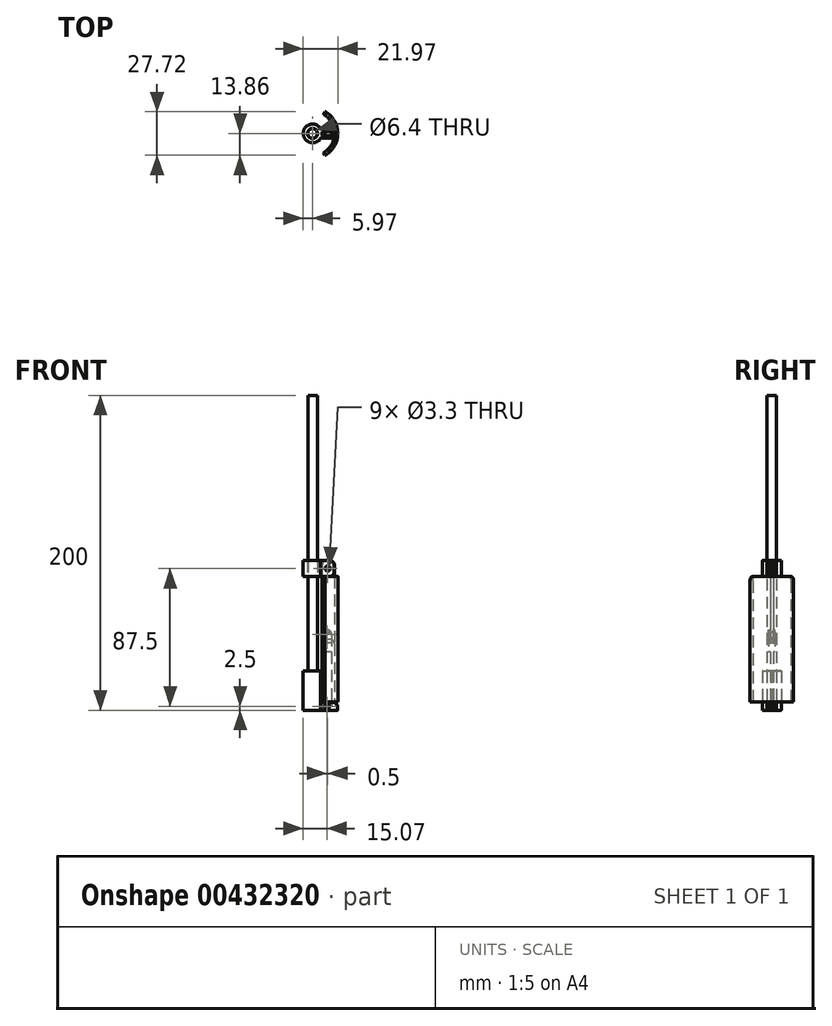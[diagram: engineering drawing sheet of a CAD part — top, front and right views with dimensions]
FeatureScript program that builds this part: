
annotation { "Feature Type Name" : "Feature", "Feature Type Description" : "" }
export const myFeature = defineFeature(function(context is Context, id is Id, definition is map)
    precondition{}
    {
        {
            var Q0;
            Q0=qCreatedBy(makeId("Top.planeOp"),FACE);
            var sketch = newSketch(context, id + "F0", { "sketchPlane" : qUnion([Q0])});
            skCircle(sketch, "E0", {"center": v(0, 0) * mm, "radius": 3 * mm});
            skCircle(sketch, "E1", {"center": v(0, 0) * mm, "radius": 16 * mm});
            skLineSegment(sketch, "E2", {"start": v(0, 0) * mm, "end": v(16, 0) * mm, "construction": true});
            skLineSegment(sketch, "E3", {"start": v(15.97, 1) * mm, "end": v(5.97, 1) * mm});
            skLineSegment(sketch, "E4", {"start": v(5.97, 1) * mm, "end": v(5.97, 0) * mm});
            skLineSegment(sketch, "E5", {"start": v(15.72, 3) * mm, "end": v(0, 3) * mm});
            skCircle(sketch, "E6", {"center": v(0, 0) * mm, "radius": 5.97 * mm});
            skLineSegment(sketch, "E7.MirrorCS", {"start": v(15.97, -1) * mm, "end": v(5.97, -1) * mm});
            skLineSegment(sketch, "E8.MirrorCS", {"start": v(5.97, -1) * mm, "end": v(5.97, 0) * mm});
            skLineSegment(sketch, "E9.MirrorCS", {"start": v(15.72, -3) * mm, "end": v(0, -3) * mm});
            skSolve(sketch);
        }
        {
            var Q0;
            Q0=makeQuery(id+"F0.imprint","IMPRINT",FACE,{"disambiguationData":[TD([[makeQuery(id+"F0.imprint","IMPRINT",EDGE,{"derivedFrom":sQuery(id+"F0.wireOp",EDGE,"E0")}),1.0]])]});
            extrude(context, id + "F1", {"entities" : qUnion([Q0]), "depth" : 200 * mm});
        }
        {
            var Q0;
            Q0=makeQuery(id+"F0.imprint","IMPRINT",FACE,{"disambiguationData":[TD([[makeQuery(id+"F0.imprint","IMPRINT",EDGE,{"derivedFrom":sQuery(id+"F0.wireOp",EDGE,"E0")}),-1.0]])]});
            var Q1;
            {var subQ0=sQuery(id+"F0.wireOp",EDGE,"E7.MirrorCS");Q1=makeQuery(id+"F0.imprint","IMPRINT",FACE,{"disambiguationData":[TD([[makeQuery(id+"F0.imprint","IMPRINT",EDGE,{"derivedFrom":subQ0}),1.0]])]});}
            var Q2;
            {var subQ5=sQuery(id+"F0.wireOp",EDGE,"E3");Q2=makeQuery(id+"F0.imprint","IMPRINT",FACE,{"disambiguationData":[TD([[makeQuery(id+"F0.imprint","IMPRINT",EDGE,{"derivedFrom":subQ5}),-1.0]])]});}
            var Q3;
            {var subQ4=sQuery(id+"F0.wireOp",EDGE,"E5");var subQ5=sQuery(id+"F0.wireOp",EDGE,"E0");var subQ6=makeQuery(id+"F0.imprint","INTERSECT",VERTEX,{"derivedFrom":[subQ5,subQ4]});Q3=makeQuery(id+"F0.imprint","IMPRINT",FACE,{"disambiguationData":[TD([[makeQuery(id+"F0.imprint","IMPRINT",EDGE,{"disambiguationData":[TD([[subQ6,1.0]])],"derivedFrom":subQ5}),-1.0]])]});}
            extrude(context, id + "F2", {"entities" : qUnion([Q0, Q1, Q2, Q3]), "operationType" : NewBodyOperationType.ADD, "depth" : 5 * mm});
        }
        {
            var Q0;
            Q0=makeQuery(id+"F2.opExtrude","CAP_FACE",FACE,{"disambiguationData":[OSD([sQuery(id+"F0.wireOp",EDGE,"E0"),sQuery(id+"F0.wireOp",EDGE,"E1")])],"isStart":false});
            var sketch = newSketch(context, id + "F3", { "sketchPlane" : qUnion([Q0])});
            skCircle(sketch, "E10", {"center": v(0, 0) * mm, "radius": 16 * mm});
            skCircle(sketch, "E11", {"center": v(0, 0) * mm, "radius": 14 * mm});
            skLineSegment(sketch, "E12", {"start": v(7, 12.12) * mm, "end": v(8, 13.86) * mm});
            skLineSegment(sketch, "E13", {"start": v(0, 0) * mm, "end": v(16, 0) * mm, "construction": true});
            skLineSegment(sketch, "E14.MirrorCS", {"start": v(7, -12.12) * mm, "end": v(8, -13.86) * mm});
            skLineSegment(sketch, "E15", {"start": v(13.97, 0.95) * mm, "end": v(6.1, 0.95) * mm});
            skLineSegment(sketch, "E16", {"start": v(6.1, 0.95) * mm, "end": v(6.1, 0) * mm});
            skLineSegment(sketch, "E17.MirrorCS", {"start": v(13.97, -0.95) * mm, "end": v(6.1, -0.95) * mm});
            skLineSegment(sketch, "E18.MirrorCS", {"start": v(6.1, -0.95) * mm, "end": v(6.1, 0) * mm});
            skLineSegment(sketch, "E19", {"start": v(12.1, 0.95) * mm, "end": v(12.1, -0.95) * mm});
            skSolve(sketch);
        }
        {
            var Q0;
            {var subQ0=sQuery(id+"F3.wireOp",EDGE,"E12");Q0=makeQuery(id+"F3.imprint","IMPRINT",FACE,{"disambiguationData":[TD([[makeQuery(id+"F3.imprint","IMPRINT",EDGE,{"derivedFrom":subQ0}),-1.0]])]});}
            var Q1;
            {var subQ3=sQuery(id+"F3.wireOp",EDGE,"E14.MirrorCS");Q1=makeQuery(id+"F3.imprint","IMPRINT",FACE,{"disambiguationData":[TD([[makeQuery(id+"F3.imprint","IMPRINT",EDGE,{"derivedFrom":subQ3}),1.0]])]});}
            var Q2;
            {var subQ0=sQuery(id+"F3.wireOp",EDGE,"E10");var subQ1=makeQuery(id+"F2.opExtrude","CAP_EDGE",EDGE,{"disambiguationData":[OSD([sQuery(id+"F0.wireOp",EDGE,"E7.MirrorCS")])],"isStart":false});var subQ2=makeQuery(id+"F3.imprint","INTERSECT",VERTEX,{"derivedFrom":[subQ1,subQ0]});Q2=makeQuery(id+"F3.imprint","IMPRINT",FACE,{"disambiguationData":[TD([[makeQuery(id+"F3.imprint","IMPRINT",EDGE,{"disambiguationData":[TD([[subQ2,1.0]])],"derivedFrom":subQ0}),1.0]])]});}
            var Q3;
            {var subQ5=makeQuery(id+"F2.opExtrude","CAP_EDGE",EDGE,{"disambiguationData":[OSD([sQuery(id+"F0.wireOp",EDGE,"E3")])],"isStart":false});var subQ7=sQuery(id+"F3.wireOp",EDGE,"E10");var subQ8=makeQuery(id+"F3.imprint","INTERSECT",VERTEX,{"derivedFrom":[subQ5,subQ7]});Q3=makeQuery(id+"F3.imprint","IMPRINT",FACE,{"disambiguationData":[TD([[makeQuery(id+"F3.imprint","IMPRINT",EDGE,{"disambiguationData":[TD([[subQ8,1.0]])],"derivedFrom":subQ7}),1.0]])]});}
            var Q4;
            {var subQ0=sQuery(id+"F3.wireOp",EDGE,"E10");var subQ1=makeQuery(id+"F2.opExtrude","CAP_EDGE",EDGE,{"disambiguationData":[OSD([sQuery(id+"F0.wireOp",EDGE,"E3")])],"isStart":false});var subQ2=makeQuery(id+"F3.imprint","INTERSECT",VERTEX,{"derivedFrom":[subQ1,subQ0]});Q4=makeQuery(id+"F3.imprint","IMPRINT",FACE,{"disambiguationData":[TD([[makeQuery(id+"F3.imprint","IMPRINT",EDGE,{"disambiguationData":[TD([[subQ2,-1.0]])],"derivedFrom":subQ0}),1.0]])]});}
            extrude(context, id + "F4", {"entities" : qUnion([Q0, Q1, Q2, Q3, Q4]), "depth" : 80 * mm, "hasSecondDirection" : true, "secondDirectionOppositeDirection" : false, "secondDirectionDepth" : .2 * mm});
        }
        {
            var Q0;
            {var subQ0=sQuery(id+"F3.wireOp",EDGE,"E15");Q0=makeQuery(id+"F3.imprint","IMPRINT",FACE,{"disambiguationData":[TD([[makeQuery(id+"F3.imprint","IMPRINT",EDGE,{"derivedFrom":subQ0}),1.0]])]});}
            var Q1;
            {var subQ3=sQuery(id+"F3.wireOp",EDGE,"E16");Q1=makeQuery(id+"F3.imprint","IMPRINT",FACE,{"disambiguationData":[TD([[makeQuery(id+"F3.imprint","IMPRINT",EDGE,{"derivedFrom":subQ3}),1.0]])]});}
            extrude(context, id + "F5", {"entities" : qUnion([Q0, Q1]), "operationType" : NewBodyOperationType.ADD, "depth" : 90 * mm});
        }
        {
            var Q0;
            {var subQ0=sQuery(id+"F3.wireOp",EDGE,"E15");Q0=makeQuery(id+"F3.imprint","IMPRINT",FACE,{"disambiguationData":[TD([[makeQuery(id+"F3.imprint","IMPRINT",EDGE,{"derivedFrom":subQ0}),1.0]])]});}
            var Q1;
            {var subQ3=sQuery(id+"F3.wireOp",EDGE,"E16");Q1=makeQuery(id+"F3.imprint","IMPRINT",FACE,{"disambiguationData":[TD([[makeQuery(id+"F3.imprint","IMPRINT",EDGE,{"derivedFrom":subQ3}),1.0]])]});}
            extrude(context, id + "F6", {"entities" : qUnion([Q0, Q1]), "operationType" : NewBodyOperationType.REMOVE, "depth" : 40 * mm});
        }
        {
            var Q0;
            {var subQ3=sQuery(id+"F3.wireOp",EDGE,"E16");Q0=makeQuery(id+"F3.imprint","IMPRINT",FACE,{"disambiguationData":[TD([[makeQuery(id+"F3.imprint","IMPRINT",EDGE,{"derivedFrom":subQ3}),1.0]])]});}
            extrude(context, id + "F7", {"entities" : qUnion([Q0]), "depth" : 38 * mm, "hasSecondDirection" : true, "secondDirectionOppositeDirection" : true, "secondDirectionDepth" : 5 * mm});
        }
        {
            var Q0;
            Q0=makeQuery(id+"F2.opExtrude","CAP_FACE",FACE,{"disambiguationData":[OSD([sQuery(id+"F0.wireOp",EDGE,"E0"),sQuery(id+"F0.wireOp",EDGE,"E1")])],"isStart":false});
            var sketch = newSketch(context, id + "F8", { "sketchPlane" : qUnion([Q0])});
            skLineSegment(sketch, "E20", {"start": v(14, 0) * mm, "end": v(14, 1) * mm, "construction": true});
            skLineSegment(sketch, "E21", {"start": v(14, 1) * mm, "end": v(6, 1) * mm});
            skLineSegment(sketch, "E22", {"start": v(6, 1) * mm, "end": v(6, 0) * mm});
            skLineSegment(sketch, "E23", {"start": v(14, 1) * mm, "end": v(14, 3) * mm});
            skLineSegment(sketch, "E24", {"start": v(0, 3) * mm, "end": v(0, 0) * mm});
            skLineSegment(sketch, "E25", {"start": v(14, 3) * mm, "end": v(6, 3) * mm});
            skLineSegment(sketch, "E26", {"start": v(6, 3) * mm, "end": v(0, 3) * mm});
            skPoint(sketch, "E27", {"position": v(10, 3) * mm});
            skLineSegment(sketch, "E28", {"start": v(0, 0) * mm, "end": v(6, 0) * mm, "construction": true});
            skLineSegment(sketch, "E29.MirrorCS", {"start": v(6, -1) * mm, "end": v(6, 0) * mm});
            skLineSegment(sketch, "E30.MirrorCS", {"start": v(14, -1) * mm, "end": v(6, -1) * mm});
            skLineSegment(sketch, "E31.MirrorCS", {"start": v(14, -1) * mm, "end": v(14, -3) * mm});
            skLineSegment(sketch, "E32.MirrorCS", {"start": v(14, -3) * mm, "end": v(6, -3) * mm});
            skLineSegment(sketch, "E33.MirrorCS", {"start": v(6, -3) * mm, "end": v(0, -3) * mm});
            skLineSegment(sketch, "E34.MirrorCS", {"start": v(0, -3) * mm, "end": v(0, 0) * mm});
            skCircle(sketch, "E35", {"center": v(0, 0) * mm, "radius": 14 * mm});
            skCircle(sketch, "E36", {"center": v(0, 0) * mm, "radius": 3.2 * mm});
            skLineSegment(sketch, "E37", {"start": v(6, 3) * mm, "end": v(6, 1) * mm});
            skLineSegment(sketch, "E38.MirrorCS", {"start": v(6, -3) * mm, "end": v(6, -1) * mm});
            skCircle(sketch, "E39", {"center": v(0, 0) * mm, "radius": 6 * mm});
            skSolve(sketch);
        }
        {
            var Q0;
            {var subQ0=sQuery(id+"F8.wireOp",EDGE,"E38.MirrorCS");Q0=makeQuery(id+"F8.imprint","IMPRINT",FACE,{"disambiguationData":[TD([[makeQuery(id+"F8.imprint","IMPRINT",EDGE,{"derivedFrom":subQ0}),-1.0]])]});}
            var Q1;
            {var subQ0=sQuery(id+"F8.wireOp",EDGE,"E38.MirrorCS");Q1=makeQuery(id+"F8.imprint","IMPRINT",FACE,{"disambiguationData":[TD([[makeQuery(id+"F8.imprint","IMPRINT",EDGE,{"derivedFrom":subQ0}),1.0]])]});}
            var Q2;
            {var subQ1=makeQuery(id+"F2.opExtrude","CAP_EDGE",EDGE,{"disambiguationData":[OSD([sQuery(id+"F0.wireOp",EDGE,"E6")])],"isStart":false});var subQ5=sQuery(id+"F8.wireOp",EDGE,"E26");var subQ6=makeQuery(id+"F8.imprint","INTERSECT",VERTEX,{"derivedFrom":[subQ1,subQ5]});Q2=makeQuery(id+"F8.imprint","IMPRINT",FACE,{"disambiguationData":[TD([[makeQuery(id+"F8.imprint","IMPRINT",EDGE,{"disambiguationData":[TD([[subQ6,-1.0]])],"derivedFrom":subQ5}),1.0]])]});}
            var Q3;
            {var subQ1=makeQuery(id+"F2.opExtrude","CAP_EDGE",EDGE,{"disambiguationData":[OSD([sQuery(id+"F0.wireOp",EDGE,"E6")])],"isStart":false});Q3=makeQuery(id+"F8.imprint","IMPRINT",FACE,{"disambiguationData":[TD([[makeQuery(id+"F8.imprint","IMPRINT",EDGE,{"derivedFrom":subQ1}),1.0]])]});}
            var Q4;
            {var subQ0=sQuery(id+"F8.wireOp",EDGE,"E37");Q4=makeQuery(id+"F8.imprint","IMPRINT",FACE,{"disambiguationData":[TD([[makeQuery(id+"F8.imprint","IMPRINT",EDGE,{"derivedFrom":subQ0}),1.0]])]});}
            var Q5;
            {var subQ3=sQuery(id+"F8.wireOp",EDGE,"E37");Q5=makeQuery(id+"F8.imprint","IMPRINT",FACE,{"disambiguationData":[TD([[makeQuery(id+"F8.imprint","IMPRINT",EDGE,{"derivedFrom":subQ3}),-1.0]])]});}
            extrude(context, id + "F9", {"entities" : qUnion([Q0, Q1, Q2, Q3, Q4, Q5]), "depth" : 10 * mm});
        }
        {
            var Q0;
            Q0=makeQuery(id+"F9.opExtrude","SWEPT_BODY",BODY,{"disambiguationData":[OSD([sQuery(id+"F8.wireOp",EDGE,"E21"),sQuery(id+"F8.wireOp",EDGE,"E22"),sQuery(id+"F8.wireOp",EDGE,"E24"),sQuery(id+"F8.wireOp",EDGE,"E25"),sQuery(id+"F8.wireOp",EDGE,"E26"),sQuery(id+"F8.wireOp",EDGE,"E29.MirrorCS"),sQuery(id+"F8.wireOp",EDGE,"E30.MirrorCS"),sQuery(id+"F8.wireOp",EDGE,"E32.MirrorCS"),sQuery(id+"F8.wireOp",EDGE,"E33.MirrorCS"),sQuery(id+"F8.wireOp",EDGE,"E34.MirrorCS"),sQuery(id+"F8.wireOp",EDGE,"E35"),sQuery(id+"F8.wireOp",EDGE,"E36")])]});
            transform(context, id + "F10", {"entities" : qUnion([Q0]), "transformType" : TransformType.TRANSLATION_3D, "dx" : 0 * mm, "dy" : 0 * mm, "dz" : 80 * mm, "makeCopy" : false});
        }
        {
            var Q0;
            Q0=makeQuery(id+"F7.opExtrude","SWEPT_FACE",FACE,{"disambiguationData":[OSD([sQuery(id+"F3.wireOp",EDGE,"E15")])]});
            var sketch = newSketch(context, id + "F11", { "sketchPlane" : qUnion([Q0])});
            skLineSegment(sketch, "E40", {"start": v(-12.1, 37) * mm, "end": v(-6.1, 37) * mm});
            skSolve(sketch);
        }
        {
            var Q0;
            {var subQ0=sQuery(id+"F11.wireOp",EDGE,"E40");Q0=makeQuery(id+"F11.imprint","IMPRINT",FACE,{"disambiguationData":[TD([[makeQuery(id+"F11.imprint","IMPRINT",EDGE,{"derivedFrom":subQ0}),1.0]])]});}
            extrude(context, id + "F12", {"entities" : qUnion([Q0]), "operationType" : NewBodyOperationType.ADD, "depth" : 1 * mm, "hasSecondDirection" : true, "secondDirectionOppositeDirection" : true, "secondDirectionDepth" : 3 * mm});
        }
        {
            var Q0;
            {var subQ0=sQuery(id+"F3.wireOp",EDGE,"E15");Q0=makeQuery(id+"F12.boolean.opBoolean","MERGE",FACE,{"derivedFrom":[makeQuery(id+"F7.opExtrude","CAP_FACE",FACE,{"disambiguationData":[OSD([subQ0,sQuery(id+"F3.wireOp",EDGE,"E16"),sQuery(id+"F3.wireOp",EDGE,"E17.MirrorCS"),sQuery(id+"F3.wireOp",EDGE,"E18.MirrorCS"),sQuery(id+"F3.wireOp",EDGE,"E19")])],"isStart":false}),makeQuery(id+"F12.opExtrude","SWEPT_FACE",FACE,{"disambiguationData":[OSD([subQ0])]})]});}
            var sketch = newSketch(context, id + "F13", { "sketchPlane" : qUnion([Q0])});
            skLineSegment(sketch, "E41", {"start": v(6.1, 1.05) * mm, "end": v(12.1, 1.05) * mm});
            skLineSegment(sketch, "E42", {"start": v(6.1, -0.05) * mm, "end": v(12.1, -0.05) * mm, "construction": true});
            skLineSegment(sketch, "E43.MirrorCS", {"start": v(6.1, -1.15) * mm, "end": v(12.1, -1.15) * mm});
            skSolve(sketch);
        }
        {
            var Q0;
            {var subQ0=sQuery(id+"F13.wireOp",EDGE,"E41");Q0=makeQuery(id+"F13.imprint","IMPRINT",FACE,{"disambiguationData":[TD([[makeQuery(id+"F13.imprint","IMPRINT",EDGE,{"derivedFrom":subQ0}),1.0]])]});}
            var Q1;
            {var subQ0=sQuery(id+"F13.wireOp",EDGE,"E43.MirrorCS");Q1=makeQuery(id+"F13.imprint","IMPRINT",FACE,{"disambiguationData":[TD([[makeQuery(id+"F13.imprint","IMPRINT",EDGE,{"derivedFrom":subQ0}),-1.0]])]});}
            extrude(context, id + "F14", {"entities" : qUnion([Q0, Q1]), "operationType" : NewBodyOperationType.ADD, "depth" : 8 * mm});
        }
        {
            var Q0;
            {var subQ0=sQuery(id+"F3.wireOp",EDGE,"E15");Q0=makeQuery(id+"F14.boolean.opBoolean","MERGE",FACE,{"derivedFrom":[makeQuery(id+"F12.opExtrude","CAP_FACE",FACE,{"disambiguationData":[OSD([subQ0,sQuery(id+"F3.wireOp",EDGE,"E16"),sQuery(id+"F3.wireOp",EDGE,"E19"),sQuery(id+"F11.wireOp",EDGE,"E40")])],"isStart":false}),makeQuery(id+"F14.opExtrude","SWEPT_FACE",FACE,{"disambiguationData":[OSD([subQ0]),TDD([makeQuery(id+"F13.imprint","IMPRINT",EDGE,{"derivedFrom":makeQuery(id+"F12.opExtrude","CAP_EDGE",EDGE,{"disambiguationData":[OSD([subQ0])],"isStart":false})})])]})]});}
            var sketch = newSketch(context, id + "F15", { "sketchPlane" : qUnion([Q0])});
            skPoint(sketch, "E44", {"position": v(-9.1, 48) * mm});
            skPoint(sketch, "E44.positionSnap0", {"position": v(-9.1, 51) * mm});
            skSolve(sketch);
        }
        {
            var Q0;
            Q0=sQuery(id+"F15.wireOp",VERTEX,"E44");
            var Q1;
            Q1=makeQuery(id+"F7.opExtrude","SWEPT_BODY",BODY,{"disambiguationData":[OSD([sQuery(id+"F3.wireOp",EDGE,"E15"),sQuery(id+"F3.wireOp",EDGE,"E16"),sQuery(id+"F3.wireOp",EDGE,"E17.MirrorCS"),sQuery(id+"F3.wireOp",EDGE,"E18.MirrorCS"),sQuery(id+"F3.wireOp",EDGE,"E19")])]});
            hole(context, id + "F16", {"style" : HoleStyle.SIMPLE, "endStyle" : HoleEndStyle.THROUGH, "standardTappedOrClearance" : lookupTablePath({ "standard" : "ISO", "fit" : "Normal", "size" : "M3", "type" : "Clearance" }), "standardBlindInLast" : lookupTablePath({ "fit" : "Standard", "standard" : "ISO", "size" : "M3", "type" : "Clearance" }), "holeDiameter" : 3.3 * mm, "isTappedThrough" : true, "tappedDepth" : 12 * mm, "tapClearance" : 3, "locations" : qUnion([Q0]), "scope" : qUnion([Q1])});
        }
        {
            var Q0;
            Q0=makeQuery(id+"F0.imprint","IMPRINT",FACE,{"disambiguationData":[TD([[makeQuery(id+"F0.imprint","IMPRINT",EDGE,{"derivedFrom":sQuery(id+"F0.wireOp",EDGE,"E0")}),-1.0]])]});
            var sketch = newSketch(context, id + "F17", { "sketchPlane" : qUnion([Q0])});
            skLineSegment(sketch, "E45", {"start": v(0, 0) * mm, "end": v(16, 0) * mm});
            skLineSegment(sketch, "E46", {"start": v(16, 0) * mm, "end": v(16, -1) * mm});
            skLineSegment(sketch, "E47", {"start": v(16, -1) * mm, "end": v(6, -1) * mm});
            skLineSegment(sketch, "E48", {"start": v(6, -1) * mm, "end": v(6, 0) * mm});
            skLineSegment(sketch, "E49.MirrorCS", {"start": v(6, 1) * mm, "end": v(6, 0) * mm});
            skLineSegment(sketch, "E50.MirrorCS", {"start": v(16, 1) * mm, "end": v(6, 1) * mm});
            skLineSegment(sketch, "E51.MirrorCS", {"start": v(16, 0) * mm, "end": v(16, 1) * mm});
            skSolve(sketch);
        }
        {
            var Q0;
            {var subQ3=sQuery(id+"F17.wireOp",EDGE,"E48");Q0=makeQuery(id+"F17.imprint","IMPRINT",FACE,{"disambiguationData":[TD([[makeQuery(id+"F17.imprint","IMPRINT",EDGE,{"derivedFrom":subQ3}),-1.0]])]});}
            var Q1;
            {var subQ3=sQuery(id+"F17.wireOp",EDGE,"E49.MirrorCS");Q1=makeQuery(id+"F17.imprint","IMPRINT",FACE,{"disambiguationData":[TD([[makeQuery(id+"F17.imprint","IMPRINT",EDGE,{"derivedFrom":subQ3}),1.0]])]});}
            extrude(context, id + "F18", {"entities" : qUnion([Q0, Q1]), "depth" : 6 * mm});
        }
        {
            var Q0;
            Q0=makeQuery(id+"F18.opExtrude","SWEPT_BODY",BODY,{"disambiguationData":[OSD([sQuery(id+"F0.wireOp",EDGE,"E1"),sQuery(id+"F17.wireOp",EDGE,"E47"),sQuery(id+"F17.wireOp",EDGE,"E48"),sQuery(id+"F17.wireOp",EDGE,"E49.MirrorCS"),sQuery(id+"F17.wireOp",EDGE,"E50.MirrorCS")])]});
            var Q1;
            Q1=makeQuery(id+"F1.opExtrude","SWEPT_BODY",BODY,{"disambiguationData":[OSD([sQuery(id+"F0.wireOp",EDGE,"E0")])]});
            booleanBodies(context, id + "F19", {"operationType" : BooleanOperationType.SUBTRACTION, "tools" : qUnion([Q0]), "targets" : qUnion([Q1])});
        }
        {
            var Q0;
            Q0=makeQuery(id+"F7.opExtrude","SWEPT_FACE",FACE,{"disambiguationData":[OSD([sQuery(id+"F3.wireOp",EDGE,"E17.MirrorCS")])]});
            var sketch = newSketch(context, id + "F20", { "sketchPlane" : qUnion([Q0])});
            skPoint(sketch, "E52", {"position": v(9.1, 0) * mm});
            skPoint(sketch, "E53", {"position": v(9.1, 2.5) * mm});
            skSolve(sketch);
        }
        {
            var Q0;
            Q0=sQuery(id+"F20.wireOp",VERTEX,"E53");
            var Q1;
            Q1=makeQuery(id+"F7.opExtrude","SWEPT_BODY",BODY,{"disambiguationData":[OSD([sQuery(id+"F3.wireOp",EDGE,"E15"),sQuery(id+"F3.wireOp",EDGE,"E16"),sQuery(id+"F3.wireOp",EDGE,"E17.MirrorCS"),sQuery(id+"F3.wireOp",EDGE,"E18.MirrorCS"),sQuery(id+"F3.wireOp",EDGE,"E19")])]});
            hole(context, id + "F21", {"style" : HoleStyle.SIMPLE, "endStyle" : HoleEndStyle.THROUGH, "standardTappedOrClearance" : lookupTablePath({ "standard" : "ISO", "fit" : "Normal", "size" : "M3", "type" : "Clearance" }), "standardBlindInLast" : lookupTablePath({ "fit" : "Standard", "standard" : "ISO", "size" : "M3", "type" : "Clearance" }), "holeDiameter" : 3.3 * mm, "isTappedThrough" : true, "tappedDepth" : 12 * mm, "tapClearance" : 3, "locations" : qUnion([Q0]), "scope" : qUnion([Q1])});
        }
        {
            var Q0;
            Q0=sQuery(id+"F20.wireOp",VERTEX,"E53");
            var Q1;
            Q1=makeQuery(id+"F1.opExtrude","SWEPT_BODY",BODY,{"disambiguationData":[OSD([sQuery(id+"F0.wireOp",EDGE,"E0")])]});
            hole(context, id + "F22", {"style" : HoleStyle.SIMPLE, "endStyle" : HoleEndStyle.THROUGH, "standardTappedOrClearance" : lookupTablePath({ "standard" : "ISO", "fit" : "Normal", "size" : "M3", "type" : "Clearance" }), "standardBlindInLast" : lookupTablePath({ "fit" : "Standard", "standard" : "ISO", "size" : "M3", "type" : "Clearance" }), "holeDiameter" : 3.3 * mm, "isTappedThrough" : true, "tappedDepth" : 12 * mm, "tapClearance" : 3, "locations" : qUnion([Q0]), "scope" : qUnion([Q1])});
        }
        {
            var Q0;
            Q0=sQuery(id+"F20.wireOp",VERTEX,"E53");
            var Q1;
            Q1=makeQuery(id+"F1.opExtrude","SWEPT_BODY",BODY,{"disambiguationData":[OSD([sQuery(id+"F0.wireOp",EDGE,"E0")])]});
            hole(context, id + "F23", {"style" : HoleStyle.SIMPLE, "endStyle" : HoleEndStyle.THROUGH, "oppositeDirection" : true, "standardTappedOrClearance" : lookupTablePath({ "standard" : "ISO", "fit" : "Normal", "size" : "M3", "type" : "Clearance" }), "standardBlindInLast" : lookupTablePath({ "fit" : "Standard", "standard" : "ISO", "size" : "M3", "type" : "Clearance" }), "holeDiameter" : 3.3 * mm, "isTappedThrough" : true, "tappedDepth" : 12 * mm, "tapClearance" : 3, "locations" : qUnion([Q0]), "scope" : qUnion([Q1])});
        }
        {
            var Q0;
            Q0=sQuery(id+"F15.wireOp",VERTEX,"E44");
            var Q1;
            Q1=makeQuery(id+"F4.opExtrude","SWEPT_BODY",BODY,{"disambiguationData":[OSD([sQuery(id+"F3.wireOp",EDGE,"E10"),sQuery(id+"F3.wireOp",EDGE,"E11"),sQuery(id+"F3.wireOp",EDGE,"E12"),sQuery(id+"F3.wireOp",EDGE,"E14.MirrorCS")])]});
            hole(context, id + "F24", {"style" : HoleStyle.SIMPLE, "endStyle" : HoleEndStyle.BLIND, "standardTappedOrClearance" : lookupTablePath({ "standard" : "ISO", "fit" : "Normal", "size" : "M3", "type" : "Clearance" }), "standardBlindInLast" : lookupTablePath({ "fit" : "Standard", "standard" : "ISO", "size" : "M3", "type" : "Clearance" }), "holeDiameter" : 3.3 * mm, "holeDepth" : 6 * mm, "isTappedThrough" : true, "tappedDepth" : 12 * mm, "tapClearance" : 3, "locations" : qUnion([Q0]), "scope" : qUnion([Q1])});
        }
        {
            var Q0;
            Q0=makeQuery(id+"F5.opExtrude","SWEPT_FACE",FACE,{"disambiguationData":[OSD([sQuery(id+"F3.wireOp",EDGE,"E17.MirrorCS")])]});
            var sketch = newSketch(context, id + "F25", { "sketchPlane" : qUnion([Q0])});
            skPoint(sketch, "E54", {"position": v(9.6, 90) * mm});
            skSolve(sketch);
        }
        {
            var Q0;
            Q0=sQuery(id+"F25.wireOp",VERTEX,"E54");
            var Q1;
            Q1=makeQuery(id+"F9.opExtrude","SWEPT_BODY",BODY,{"disambiguationData":[OSD([sQuery(id+"F0.wireOp",EDGE,"E3"),sQuery(id+"F0.wireOp",EDGE,"E4"),sQuery(id+"F0.wireOp",EDGE,"E6"),sQuery(id+"F0.wireOp",EDGE,"E7.MirrorCS"),sQuery(id+"F0.wireOp",EDGE,"E8.MirrorCS"),sQuery(id+"F8.wireOp",EDGE,"E21"),sQuery(id+"F8.wireOp",EDGE,"E25"),sQuery(id+"F8.wireOp",EDGE,"E26"),sQuery(id+"F8.wireOp",EDGE,"E30.MirrorCS"),sQuery(id+"F8.wireOp",EDGE,"E32.MirrorCS"),sQuery(id+"F8.wireOp",EDGE,"E33.MirrorCS"),sQuery(id+"F8.wireOp",EDGE,"E35"),sQuery(id+"F8.wireOp",EDGE,"E36")])]});
            hole(context, id + "F26", {"style" : HoleStyle.SIMPLE, "endStyle" : HoleEndStyle.BLIND, "standardTappedOrClearance" : lookupTablePath({ "standard" : "ISO", "fit" : "Normal", "size" : "M3", "type" : "Clearance" }), "standardBlindInLast" : lookupTablePath({ "fit" : "Standard", "standard" : "ISO", "size" : "M3", "type" : "Clearance" }), "holeDiameter" : 3.3 * mm, "holeDepth" : 6 * mm, "isTappedThrough" : true, "tappedDepth" : 12 * mm, "tapClearance" : 3, "locations" : qUnion([Q0]), "scope" : qUnion([Q1])});
        }
        {
            var Q0;
            Q0=sQuery(id+"F25.wireOp",VERTEX,"E54");
            var Q1;
            Q1=makeQuery(id+"F9.opExtrude","SWEPT_BODY",BODY,{"disambiguationData":[OSD([sQuery(id+"F0.wireOp",EDGE,"E3"),sQuery(id+"F0.wireOp",EDGE,"E4"),sQuery(id+"F0.wireOp",EDGE,"E6"),sQuery(id+"F0.wireOp",EDGE,"E7.MirrorCS"),sQuery(id+"F0.wireOp",EDGE,"E8.MirrorCS"),sQuery(id+"F8.wireOp",EDGE,"E21"),sQuery(id+"F8.wireOp",EDGE,"E25"),sQuery(id+"F8.wireOp",EDGE,"E26"),sQuery(id+"F8.wireOp",EDGE,"E30.MirrorCS"),sQuery(id+"F8.wireOp",EDGE,"E32.MirrorCS"),sQuery(id+"F8.wireOp",EDGE,"E33.MirrorCS"),sQuery(id+"F8.wireOp",EDGE,"E35"),sQuery(id+"F8.wireOp",EDGE,"E36")])]});
            hole(context, id + "F27", {"style" : HoleStyle.SIMPLE, "endStyle" : HoleEndStyle.BLIND, "oppositeDirection" : true, "standardTappedOrClearance" : lookupTablePath({ "standard" : "ISO", "fit" : "Normal", "size" : "M3", "type" : "Clearance" }), "standardBlindInLast" : lookupTablePath({ "fit" : "Standard", "standard" : "ISO", "size" : "M3", "type" : "Clearance" }), "holeDiameter" : 3.3 * mm, "holeDepth" : 6 * mm, "isTappedThrough" : true, "tappedDepth" : 12 * mm, "tapClearance" : 3, "locations" : qUnion([Q0]), "scope" : qUnion([Q1])});
        }
        {
            var Q0;
            Q0=sQuery(id+"F25.wireOp",VERTEX,"E54");
            var Q1;
            Q1=makeQuery(id+"F4.opExtrude","SWEPT_BODY",BODY,{"disambiguationData":[OSD([sQuery(id+"F3.wireOp",EDGE,"E10"),sQuery(id+"F3.wireOp",EDGE,"E11"),sQuery(id+"F3.wireOp",EDGE,"E12"),sQuery(id+"F3.wireOp",EDGE,"E14.MirrorCS")])]});
            hole(context, id + "F28", {"style" : HoleStyle.SIMPLE, "endStyle" : HoleEndStyle.BLIND, "standardTappedOrClearance" : lookupTablePath({ "standard" : "ISO", "fit" : "Normal", "size" : "M3", "type" : "Clearance" }), "standardBlindInLast" : lookupTablePath({ "fit" : "Standard", "standard" : "ISO", "size" : "M3", "type" : "Clearance" }), "holeDiameter" : 3.3 * mm, "holeDepth" : 6 * mm, "isTappedThrough" : true, "tappedDepth" : 12 * mm, "tapClearance" : 3, "locations" : qUnion([Q0]), "scope" : qUnion([Q1])});
        }
        {
            var Q0;
            Q0=makeQuery(id+"F5.opExtrude","CAP_EDGE",EDGE,{"disambiguationData":[OSD([sQuery(id+"F3.wireOp",EDGE,"E11")])],"isStart":false});
            var Q1;
            Q1=makeQuery(id+"F5.opExtrude","CAP_EDGE",EDGE,{"disambiguationData":[OSD([sQuery(id+"F3.wireOp",EDGE,"E16"),sQuery(id+"F3.wireOp",EDGE,"E18.MirrorCS")])],"isStart":false});
            var Q2;
            {var subQ0=sQuery(id+"F8.wireOp",EDGE,"E35");Q2=makeQuery(id+"F9.opExtrude","CAP_EDGE",EDGE,{"disambiguationData":[OSD([subQ0]),TDD([makeQuery(id+"F8.imprint","IMPRINT",EDGE,{"disambiguationData":[TD([[makeQuery(id+"F8.imprint","INTERSECT",VERTEX,{"derivedFrom":[sQuery(id+"F8.wireOp",EDGE,"E30.MirrorCS"),subQ0]}),1.0]])],"derivedFrom":subQ0})])],"isStart":false});}
            var Q3;
            {var subQ0=sQuery(id+"F8.wireOp",EDGE,"E35");Q3=makeQuery(id+"F9.opExtrude","CAP_EDGE",EDGE,{"disambiguationData":[OSD([subQ0]),TDD([makeQuery(id+"F8.imprint","IMPRINT",EDGE,{"disambiguationData":[TD([[makeQuery(id+"F8.imprint","INTERSECT",VERTEX,{"derivedFrom":[sQuery(id+"F8.wireOp",EDGE,"E21"),subQ0]}),-1.0]])],"derivedFrom":subQ0})])],"isStart":false});}
            var Q4;
            {var subQ0=sQuery(id+"F8.wireOp",EDGE,"E35");Q4=makeQuery(id+"F9.opExtrude","CAP_EDGE",EDGE,{"disambiguationData":[OSD([subQ0]),TDD([makeQuery(id+"F8.imprint","IMPRINT",EDGE,{"disambiguationData":[TD([[makeQuery(id+"F8.imprint","INTERSECT",VERTEX,{"derivedFrom":[sQuery(id+"F8.wireOp",EDGE,"E30.MirrorCS"),subQ0]}),1.0]])],"derivedFrom":subQ0})])],"isStart":true});}
            var Q5;
            {var subQ0=sQuery(id+"F8.wireOp",EDGE,"E35");Q5=makeQuery(id+"F9.opExtrude","CAP_EDGE",EDGE,{"disambiguationData":[OSD([subQ0]),TDD([makeQuery(id+"F8.imprint","IMPRINT",EDGE,{"disambiguationData":[TD([[makeQuery(id+"F8.imprint","INTERSECT",VERTEX,{"derivedFrom":[sQuery(id+"F8.wireOp",EDGE,"E21"),subQ0]}),-1.0]])],"derivedFrom":subQ0})])],"isStart":true});}
            var Q6;
            {var subQ0=sQuery(id+"F3.wireOp",EDGE,"E16");var subQ1=sQuery(id+"F3.wireOp",EDGE,"E15");var subQ2=sQuery(id+"F3.wireOp",EDGE,"E18.MirrorCS");var subQ3=makeQuery(id+"F12.boolean.opBoolean","MERGE",EDGE,{"derivedFrom":[makeQuery(id+"F7.opExtrude","CAP_EDGE",EDGE,{"disambiguationData":[OSD([subQ0,subQ2])],"isStart":false}),makeQuery(id+"F12.opExtrude","SWEPT_EDGE",EDGE,{"disambiguationData":[OSD([subQ1,subQ0])]})]});Q6=makeQuery(id+"F14.opExtrude","CAP_EDGE",EDGE,{"disambiguationData":[OSD([subQ1,subQ0,subQ2]),TDD([makeQuery(id+"F13.imprint","IMPRINT",EDGE,{"disambiguationData":[TD([[makeQuery(id+"F13.imprint","INTERSECT",VERTEX,{"derivedFrom":[makeQuery(id+"F12.opExtrude","CAP_EDGE",EDGE,{"disambiguationData":[OSD([subQ1])],"isStart":true}),subQ3]}),1.0]])],"derivedFrom":subQ3})])],"isStart":false});}
            var Q7;
            {var subQ0=sQuery(id+"F3.wireOp",EDGE,"E19");var subQ1=sQuery(id+"F3.wireOp",EDGE,"E15");var subQ2=makeQuery(id+"F12.boolean.opBoolean","MERGE",EDGE,{"derivedFrom":[makeQuery(id+"F7.opExtrude","CAP_EDGE",EDGE,{"disambiguationData":[OSD([subQ0])],"isStart":false}),makeQuery(id+"F12.opExtrude","SWEPT_EDGE",EDGE,{"disambiguationData":[OSD([subQ1,subQ0])]})]});Q7=makeQuery(id+"F14.opExtrude","CAP_EDGE",EDGE,{"disambiguationData":[OSD([subQ1,subQ0]),TDD([makeQuery(id+"F13.imprint","IMPRINT",EDGE,{"disambiguationData":[TD([[makeQuery(id+"F13.imprint","INTERSECT",VERTEX,{"derivedFrom":[makeQuery(id+"F12.opExtrude","CAP_EDGE",EDGE,{"disambiguationData":[OSD([subQ1])],"isStart":true}),subQ2]}),1.0]])],"derivedFrom":subQ2})])],"isStart":false});}
            var Q8;
            {var subQ0=sQuery(id+"F3.wireOp",EDGE,"E19");var subQ1=sQuery(id+"F3.wireOp",EDGE,"E15");var subQ2=makeQuery(id+"F12.boolean.opBoolean","MERGE",EDGE,{"derivedFrom":[makeQuery(id+"F7.opExtrude","CAP_EDGE",EDGE,{"disambiguationData":[OSD([subQ0])],"isStart":false}),makeQuery(id+"F12.opExtrude","SWEPT_EDGE",EDGE,{"disambiguationData":[OSD([subQ1,subQ0])]})]});Q8=makeQuery(id+"F14.opExtrude","CAP_EDGE",EDGE,{"disambiguationData":[OSD([subQ1,subQ0]),TDD([makeQuery(id+"F13.imprint","IMPRINT",EDGE,{"disambiguationData":[TD([[makeQuery(id+"F13.imprint","INTERSECT",VERTEX,{"derivedFrom":[makeQuery(id+"F12.opExtrude","CAP_EDGE",EDGE,{"disambiguationData":[OSD([subQ1])],"isStart":false}),subQ2]}),-1.0]])],"derivedFrom":subQ2})])],"isStart":false});}
            var Q9;
            {var subQ0=sQuery(id+"F3.wireOp",EDGE,"E16");var subQ1=sQuery(id+"F3.wireOp",EDGE,"E15");var subQ2=sQuery(id+"F3.wireOp",EDGE,"E18.MirrorCS");var subQ3=makeQuery(id+"F12.boolean.opBoolean","MERGE",EDGE,{"derivedFrom":[makeQuery(id+"F7.opExtrude","CAP_EDGE",EDGE,{"disambiguationData":[OSD([subQ0,subQ2])],"isStart":false}),makeQuery(id+"F12.opExtrude","SWEPT_EDGE",EDGE,{"disambiguationData":[OSD([subQ1,subQ0])]})]});Q9=makeQuery(id+"F14.opExtrude","CAP_EDGE",EDGE,{"disambiguationData":[OSD([subQ1,subQ0,subQ2]),TDD([makeQuery(id+"F13.imprint","IMPRINT",EDGE,{"disambiguationData":[TD([[makeQuery(id+"F13.imprint","INTERSECT",VERTEX,{"derivedFrom":[makeQuery(id+"F12.opExtrude","CAP_EDGE",EDGE,{"disambiguationData":[OSD([subQ1])],"isStart":false}),subQ3]}),-1.0]])],"derivedFrom":subQ3})])],"isStart":false});}
            var Q10;
            Q10=makeQuery(id+"F6.boolean.opBoolean","COPY",EDGE,{"derivedFrom":makeQuery(id+"F6.opExtrude","CAP_EDGE",EDGE,{"disambiguationData":[OSD([sQuery(id+"F3.wireOp",EDGE,"E16"),sQuery(id+"F3.wireOp",EDGE,"E18.MirrorCS")])],"isStart":false})});
            var Q11;
            Q11=makeQuery(id+"F7.opExtrude","CAP_EDGE",EDGE,{"disambiguationData":[OSD([sQuery(id+"F3.wireOp",EDGE,"E19")])],"isStart":true});
            var Q12;
            Q12=makeQuery(id+"F7.opExtrude","CAP_EDGE",EDGE,{"disambiguationData":[OSD([sQuery(id+"F3.wireOp",EDGE,"E16"),sQuery(id+"F3.wireOp",EDGE,"E18.MirrorCS")])],"isStart":true});
            var Q13;
            {var subQ0=sQuery(id+"F0.wireOp",EDGE,"E1");Q13=makeQuery(id+"F2.opExtrude","CAP_EDGE",EDGE,{"disambiguationData":[OSD([subQ0]),TDD([makeQuery(id+"F0.imprint","IMPRINT",EDGE,{"disambiguationData":[TD([[makeQuery(id+"F0.imprint","INTERSECT",VERTEX,{"derivedFrom":[subQ0,sQuery(id+"F0.wireOp",EDGE,"E3")]}),-1.0]])],"derivedFrom":subQ0})])],"isStart":false});}
            var Q14;
            {var subQ0=sQuery(id+"F0.wireOp",EDGE,"E1");Q14=makeQuery(id+"F2.opExtrude","CAP_EDGE",EDGE,{"disambiguationData":[OSD([subQ0]),TDD([makeQuery(id+"F0.imprint","IMPRINT",EDGE,{"disambiguationData":[TD([[makeQuery(id+"F0.imprint","INTERSECT",VERTEX,{"derivedFrom":[subQ0,sQuery(id+"F0.wireOp",EDGE,"E7.MirrorCS")]}),1.0]])],"derivedFrom":subQ0})])],"isStart":false});}
            var Q15;
            Q15=makeQuery(id+"F4.opExtrude","CAP_EDGE",EDGE,{"disambiguationData":[OSD([sQuery(id+"F3.wireOp",EDGE,"E12")])],"isStart":false});
            var Q16;
            Q16=makeQuery(id+"F4.opExtrude","CAP_EDGE",EDGE,{"disambiguationData":[OSD([sQuery(id+"F3.wireOp",EDGE,"E14.MirrorCS")])],"isStart":false});
            var Q17;
            Q17=makeQuery(id+"F6.boolean.opBoolean","COPY",EDGE,{"derivedFrom":makeQuery(id+"F6.opExtrude","CAP_EDGE",EDGE,{"disambiguationData":[OSD([sQuery(id+"F3.wireOp",EDGE,"E11")])],"isStart":false})});
            fillet(context, id + "F29", {"entities" : qUnion([Q0, Q1, Q2, Q3, Q4, Q5, Q6, Q7, Q8, Q9, Q10, Q11, Q12, Q13, Q14, Q15, Q16, Q17]), "radius" : 3 * mm, "tangentPropagation" : true, "allowEdgeOverflow" : false});
        }
        {
            var Q0;
            {var subQ0=sQuery(id+"F8.wireOp",EDGE,"E26");var subQ3=sQuery(id+"F8.wireOp",EDGE,"E36");var subQ4=makeQuery(id+"F8.imprint","INTERSECT",VERTEX,{"derivedFrom":[subQ0,subQ3]});Q0=makeQuery(id+"F8.imprint","IMPRINT",FACE,{"disambiguationData":[TD([[makeQuery(id+"F8.imprint","IMPRINT",EDGE,{"disambiguationData":[TD([[subQ4,-1.0]])],"derivedFrom":subQ3}),1.0]])]});}
            var Q1;
            {var subQ0=sQuery(id+"F8.wireOp",EDGE,"E26");var subQ3=sQuery(id+"F8.wireOp",EDGE,"E36");var subQ4=makeQuery(id+"F8.imprint","INTERSECT",VERTEX,{"derivedFrom":[subQ0,subQ3]});Q1=makeQuery(id+"F8.imprint","IMPRINT",FACE,{"disambiguationData":[TD([[makeQuery(id+"F8.imprint","IMPRINT",EDGE,{"disambiguationData":[TD([[subQ4,1.0]])],"derivedFrom":subQ3}),1.0]])]});}
            var Q2;
            {var subQ1=makeQuery(id+"F2.opExtrude","CAP_EDGE",EDGE,{"disambiguationData":[OSD([sQuery(id+"F0.wireOp",EDGE,"E6")])],"isStart":false});var subQ5=sQuery(id+"F8.wireOp",EDGE,"E26");var subQ6=makeQuery(id+"F8.imprint","INTERSECT",VERTEX,{"derivedFrom":[subQ1,subQ5]});Q2=makeQuery(id+"F8.imprint","IMPRINT",FACE,{"disambiguationData":[TD([[makeQuery(id+"F8.imprint","IMPRINT",EDGE,{"disambiguationData":[TD([[subQ6,-1.0]])],"derivedFrom":subQ5}),1.0]])]});}
            var Q3;
            {var subQ1=makeQuery(id+"F2.opExtrude","CAP_EDGE",EDGE,{"disambiguationData":[OSD([sQuery(id+"F0.wireOp",EDGE,"E6")])],"isStart":false});Q3=makeQuery(id+"F8.imprint","IMPRINT",FACE,{"disambiguationData":[TD([[makeQuery(id+"F8.imprint","IMPRINT",EDGE,{"derivedFrom":subQ1}),1.0]])]});}
            extrude(context, id + "F30", {"entities" : qUnion([Q0, Q1, Q2, Q3]), "operationType" : NewBodyOperationType.ADD, "depth" : 20 * mm});
        }
    });
